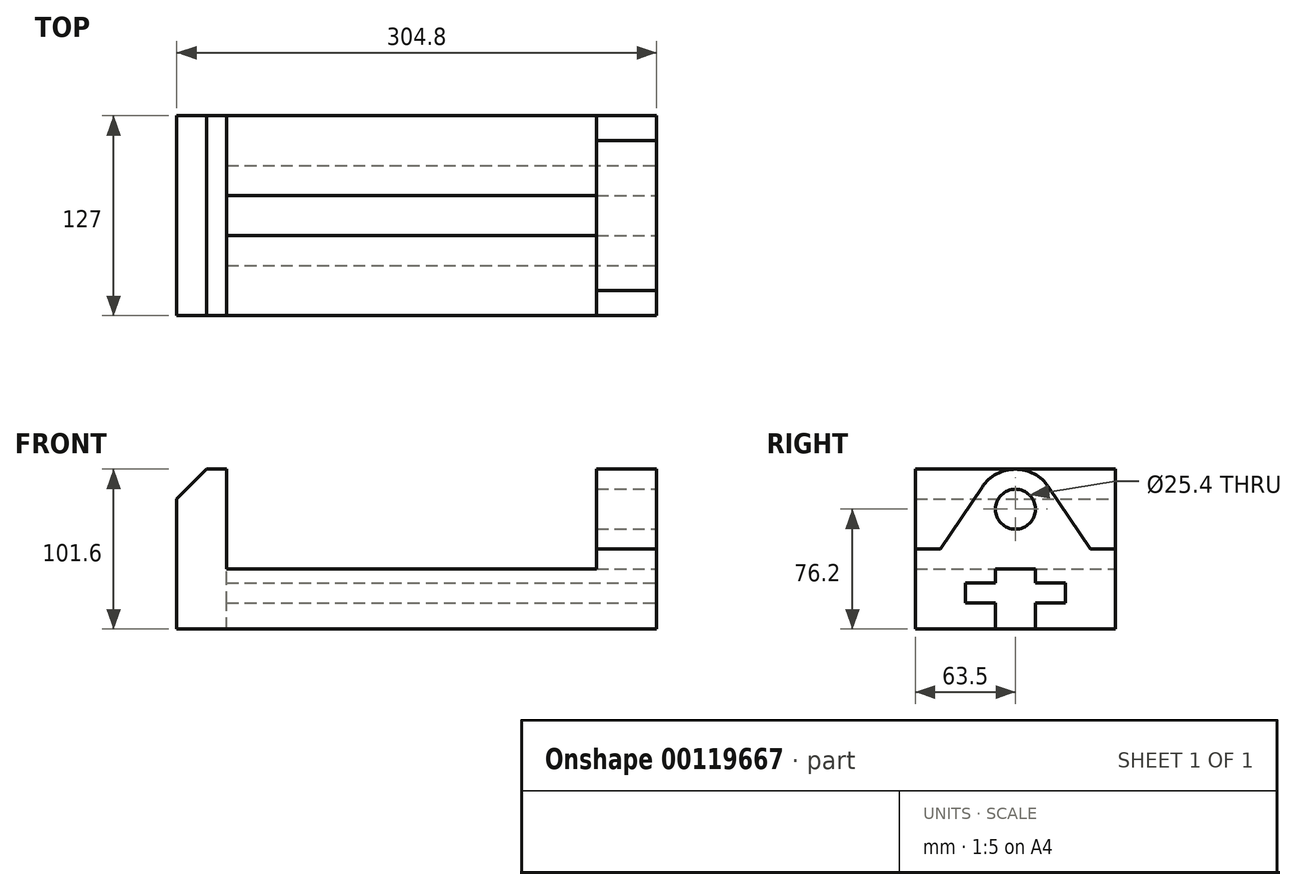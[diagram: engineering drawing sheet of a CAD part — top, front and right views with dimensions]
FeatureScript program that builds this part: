
annotation { "Feature Type Name" : "Feature", "Feature Type Description" : "" }
export const myFeature = defineFeature(function(context is Context, id is Id, definition is map)
    precondition{}
    {
        {
            var Q0;
            Q0=qCreatedBy(makeId("Front.planeOp"),FACE);
            var sketch = newSketch(context, id + "F0", { "sketchPlane" : qUnion([Q0])});
            skLineSegment(sketch, "E0", {"start": v(0, 0) * mm, "end": v(304.8, 0) * mm});
            skLineSegment(sketch, "E1", {"start": v(0, 0) * mm, "end": v(0, 82.55) * mm});
            skLineSegment(sketch, "E2", {"start": v(0, 82.55) * mm, "end": v(19.05, 101.6) * mm});
            skLineSegment(sketch, "E3", {"start": v(19.05, 101.6) * mm, "end": v(31.75, 101.6) * mm});
            skLineSegment(sketch, "E4", {"start": v(31.75, 101.6) * mm, "end": v(31.75, 38.1) * mm});
            skLineSegment(sketch, "E5", {"start": v(31.75, 38.1) * mm, "end": v(266.7, 38.1) * mm});
            skLineSegment(sketch, "E6", {"start": v(266.7, 38.1) * mm, "end": v(266.7, 101.6) * mm});
            skLineSegment(sketch, "E7", {"start": v(266.7, 101.6) * mm, "end": v(304.8, 101.6) * mm});
            skLineSegment(sketch, "E8", {"start": v(304.8, 101.6) * mm, "end": v(304.8, 0) * mm});
            skSolve(sketch);
        }
        {
            var Q0;
            Q0 = qSketchRegion(id + "F0", true);
            extrude(context, id + "F1", {"entities" : qUnion([Q0]), "depth" : 127 * mm});
        }
        {
            var Q0;
            Q0=makeQuery(id+"F1.opExtrude","SWEPT_FACE",FACE,{"disambiguationData":[OSD([sQuery(id+"F0.wireOp",EDGE,"E8")])]});
            var sketch = newSketch(context, id + "F2", { "sketchPlane" : qUnion([Q0])});
            skLineSegment(sketch, "E9.bottom", {"start": v(-127, 0) * mm, "end": v(0, 0) * mm, "construction": true});
            skLineSegment(sketch, "E9.top", {"start": v(-127, 101.6) * mm, "end": v(0, 101.6) * mm, "construction": true});
            skLineSegment(sketch, "E9.left", {"start": v(-127, 0) * mm, "end": v(-127, 101.6) * mm, "construction": true});
            skLineSegment(sketch, "E9.right", {"start": v(0, 0) * mm, "end": v(0, 101.6) * mm, "construction": true});
            skLineSegment(sketch, "E10", {"start": v(-127, 0) * mm, "end": v(-127, 50.8) * mm});
            skLineSegment(sketch, "E11", {"start": v(-127, 50.8) * mm, "end": v(-111.12, 50.8) * mm});
            skLineSegment(sketch, "E12", {"start": v(-111.13, 50.8) * mm, "end": v(-84.6, 90.35) * mm});
            skArc(sketch, "E13", {"start": v(-42.4, 90.35) * mm, "mid": v(-63.5, 101.6) * mm, "end": v(-84.6, 90.35) * mm});
            skLineSegment(sketch, "E14", {"start": v(-15.87, 50.8) * mm, "end": v(-42.4, 90.35) * mm});
            skLineSegment(sketch, "E15", {"start": v(0, 50.8) * mm, "end": v(-15.87, 50.8) * mm});
            skLineSegment(sketch, "E16", {"start": v(0, 0) * mm, "end": v(0, 50.8) * mm});
            skLineSegment(sketch, "E17", {"start": v(0, 0) * mm, "end": v(-127, 0) * mm});
            skCircle(sketch, "E18", {"center": v(-63.5, 76.2) * mm, "radius": 12.7 * mm});
            skLineSegment(sketch, "E19", {"start": v(-76.2, 0) * mm, "end": v(-76.2, 16.51) * mm});
            skLineSegment(sketch, "E20", {"start": v(-76.2, 16.51) * mm, "end": v(-95.25, 16.51) * mm});
            skLineSegment(sketch, "E21", {"start": v(-95.25, 16.51) * mm, "end": v(-95.25, 29.21) * mm});
            skLineSegment(sketch, "E22", {"start": v(-95.25, 29.21) * mm, "end": v(-76.2, 29.21) * mm});
            skLineSegment(sketch, "E23", {"start": v(-76.2, 29.21) * mm, "end": v(-76.2, 38.1) * mm});
            skLineSegment(sketch, "E24", {"start": v(-76.2, 38.1) * mm, "end": v(-50.8, 38.1) * mm});
            skLineSegment(sketch, "E25", {"start": v(-50.8, 38.1) * mm, "end": v(-50.8, 29.21) * mm});
            skLineSegment(sketch, "E26", {"start": v(-50.8, 29.21) * mm, "end": v(-31.75, 29.21) * mm});
            skLineSegment(sketch, "E27", {"start": v(-31.75, 29.21) * mm, "end": v(-31.75, 16.51) * mm});
            skLineSegment(sketch, "E28", {"start": v(-31.75, 16.51) * mm, "end": v(-50.8, 16.51) * mm});
            skLineSegment(sketch, "E29", {"start": v(-50.8, 16.51) * mm, "end": v(-50.8, 0) * mm});
            skLineSegment(sketch, "E30", {"start": v(-50.8, 0) * mm, "end": v(-76.2, 0) * mm});
            skSolve(sketch);
        }
        {
            var Q0;
            {var subQ5=sQuery(id+"F2.wireOp",EDGE,"E14");Q0=makeQuery(id+"F2.imprint","IMPRINT",FACE,{"disambiguationData":[TD([[makeQuery(id+"F2.imprint","IMPRINT",EDGE,{"derivedFrom":subQ5}),-1.0]])]});}
            var Q1;
            {var subQ7=sQuery(id+"F2.wireOp",EDGE,"E11");Q1=makeQuery(id+"F2.imprint","IMPRINT",FACE,{"disambiguationData":[TD([[makeQuery(id+"F2.imprint","IMPRINT",EDGE,{"derivedFrom":subQ7}),1.0]])]});}
            var Q2;
            Q2=makeQuery(id+"F2.imprint","IMPRINT",FACE,{"disambiguationData":[TD([[makeQuery(id+"F2.imprint","IMPRINT",EDGE,{"derivedFrom":sQuery(id+"F2.wireOp",EDGE,"E18")}),1.0]])]});
            extrude(context, id + "F3", {"entities" : qUnion([Q0, Q1, Q2]), "operationType" : NewBodyOperationType.REMOVE, "oppositeDirection" : true, "depth" : 38.1 * mm});
        }
        {
            var Q0;
            Q0=makeQuery(id+"F2.imprint","IMPRINT",FACE,{"disambiguationData":[TD([[makeQuery(id+"F2.imprint","IMPRINT",EDGE,{"derivedFrom":sQuery(id+"F2.wireOp",EDGE,"E19")}),-1.0]])]});
            extrude(context, id + "F4", {"entities" : qUnion([Q0]), "operationType" : NewBodyOperationType.REMOVE, "oppositeDirection" : true, "depth" : 273.05 * mm});
        }
    });
